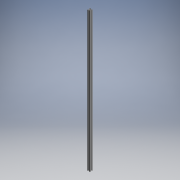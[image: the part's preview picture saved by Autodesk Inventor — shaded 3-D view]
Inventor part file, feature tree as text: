
AUTODESK INVENTOR PART (.ipt)
format: ipt  version: 2017.3 (Build 213256000, 256)  size: 210,432 bytes
history: native  units: mm (DEFAULTED — no unit token found)
features: other x21, sketch x3, hole x2, extrude x1, pattern_linear x1
ambient origin geometry x8: Origin, YZ Plane, XZ Plane, XY Plane, X Axis, Y Axis, Z Axis, Center Point
bodies: Solid1 (feature_tree)
feature tree (28):
  extrude  "Extrusion1"  Depth=1500.0mm
  hole  "Hole1"  [1 undecoded]
  hole  "Hole2"  [1 undecoded]
  pattern_linear  "Rectangular Pattern1"  [2 undecoded]
  other  "C1_XY"
  other  "C1_YZ"
  other  "C1_ZX"
  other  "C1_X"
  other  "C1_Y"
  other  "C1_Z"
  other  "C1_Center"
  other  "to_frame_cap1_XY"
  other  "to_frame_cap1_YZ"
  other  "to_frame_cap1_ZX"
  other  "to_frame_cap1_X"
  other  "to_frame_cap1_Y"
  other  "to_frame_cap1_Z"
  other  "to_frame_cap1_Center"
  other  "to_frame_cap2_XY"
  other  "to_frame_cap2_YZ"
  other  "to_frame_cap2_ZX"
  other  "to_frame_cap2_X"
  other  "to_frame_cap2_Y"
  other  "to_frame_cap2_Z"
  other  "to_frame_cap2_Center"
  sketch  "Sketch_1"  dims[d0=1500.0mm d1=0.0mm]
  sketch  "Sketch2"  dims[d2=6.8mm d3=6.0mm d4=4.0mm d5=2.0mm d6=90.0deg d7=1500.0mm d8=0.0mm]
  sketch  "Sketch3"  dims[d9=4.2mm d10=6.0mm d11=4.0mm d12=2.0mm d13=90.0deg d14=1500.0mm d15=0.0mm d16=20.0mm d18=23.2mm d19=20.0mm d21=23.2mm d22=0.0mm d23=0.0mm d24=0.0mm]
note: 4 required parameter values undecoded (feature->parameter linkage not recoverable at this tier; creation-order binding heuristic only, values carry confidence <= 0.55)
